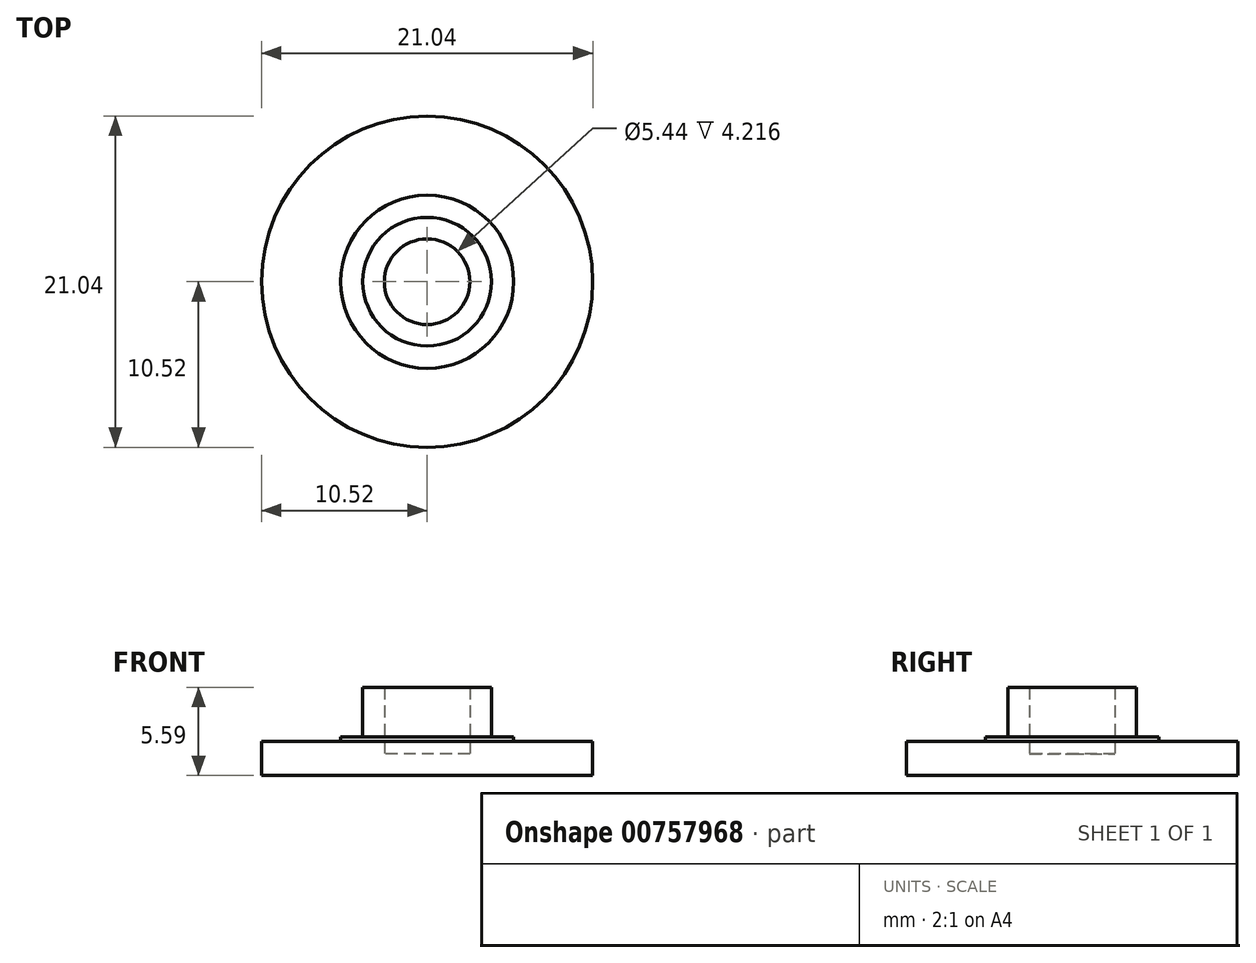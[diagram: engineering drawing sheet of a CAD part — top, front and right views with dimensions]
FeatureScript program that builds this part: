
annotation { "Feature Type Name" : "Feature", "Feature Type Description" : "" }
export const myFeature = defineFeature(function(context is Context, id is Id, definition is map)
    precondition{}
    {
        {
            var Q0;
            Q0=qCreatedBy(makeId("Top.planeOp"),FACE);
            var sketch = newSketch(context, id + "F0", { "sketchPlane" : qUnion([Q0])});
            skCircle(sketch, "E0", {"center": v(0, 0) * mm, "radius": 10.52 * mm});
            skSolve(sketch);
        }
        {
            var Q0;
            Q0 = qSketchRegion(id + "F0", true);
            extrude(context, id + "F1", {"entities" : qUnion([Q0]), "depth" : 2.16 * mm, "offsetDistance" : 25.4 * mm});
        }
        {
            var Q0;
            Q0=qCreatedBy(makeId("Top.planeOp"),FACE);
            var sketch = newSketch(context, id + "F2", { "sketchPlane" : qUnion([Q0])});
            skCircle(sketch, "E1", {"center": v(0, 0) * mm, "radius": 5.5 * mm});
            skSolve(sketch);
        }
        {
            var Q0;
            Q0 = qSketchRegion(id + "F2", true);
            extrude(context, id + "F3", {"entities" : qUnion([Q0]), "operationType" : NewBodyOperationType.ADD, "depth" : 2.44 * mm, "offsetDistance" : 25.4 * mm});
        }
        {
            var Q0;
            Q0=qCreatedBy(makeId("Top.planeOp"),FACE);
            var sketch = newSketch(context, id + "F4", { "sketchPlane" : qUnion([Q0])});
            skCircle(sketch, "E2", {"center": v(0, 0) * mm, "radius": 4.09 * mm});
            skSolve(sketch);
        }
        {
            var Q0;
            Q0 = qSketchRegion(id + "F4", true);
            extrude(context, id + "F5", {"entities" : qUnion([Q0]), "operationType" : NewBodyOperationType.ADD, "depth" : 5.6 * mm, "offsetDistance" : 25.4 * mm});
        }
        {
            var Q0;
            Q0=makeQuery(id+"F5.opExtrude","CAP_FACE",FACE,{"disambiguationData":[OSD([sQuery(id+"F4.wireOp",EDGE,"E2")])],"isStart":false});
            shell(context, id + "F6", {"entities" : qUnion([Q0]), "thickness" : 1.37 * mm});
        }
    });
